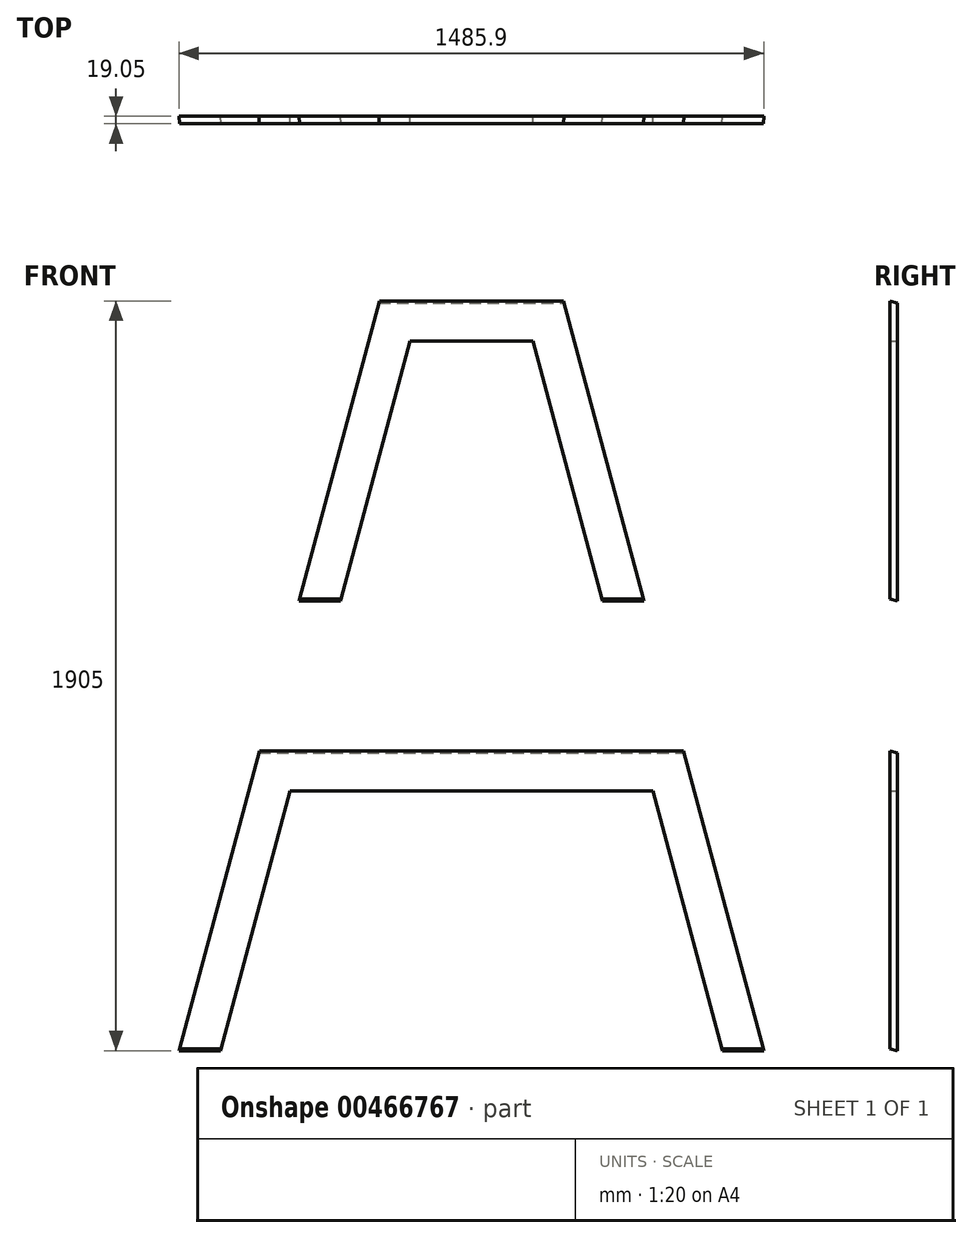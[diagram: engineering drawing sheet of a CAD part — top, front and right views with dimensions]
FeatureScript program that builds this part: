
annotation { "Feature Type Name" : "Feature", "Feature Type Description" : "" }
export const myFeature = defineFeature(function(context is Context, id is Id, definition is map)
    precondition{}
    {
        {
            var Q0;
            Q0=qCreatedBy(makeId("Front.planeOp"),FACE);
            var sketch = newSketch(context, id + "F0", { "sketchPlane" : qUnion([Q0])});
            skLineSegment(sketch, "E0", {"start": v(-742.95, -762) * mm, "end": v(-538.77, 0) * mm});
            skLineSegment(sketch, "E1", {"start": v(-538.77, 0) * mm, "end": v(0, 0) * mm});
            skLineSegment(sketch, "E2", {"start": v(-742.95, -762) * mm, "end": v(-637.77, -762) * mm});
            skLineSegment(sketch, "E3", {"start": v(-637.77, -762) * mm, "end": v(-460.81, -101.6) * mm});
            skLineSegment(sketch, "E4", {"start": v(-460.81, -101.6) * mm, "end": v(0, -101.6) * mm});
            skLineSegment(sketch, "E5", {"start": v(0, -101.6) * mm, "end": v(0, -310.28) * mm, "construction": true});
            skLineSegment(sketch, "E6.MirrorCS", {"start": v(460.81, -101.6) * mm, "end": v(0, -101.6) * mm});
            skLineSegment(sketch, "E7.MirrorCS", {"start": v(538.77, 0) * mm, "end": v(0, 0) * mm});
            skLineSegment(sketch, "E8.MirrorCS", {"start": v(742.95, -762) * mm, "end": v(538.77, 0) * mm});
            skLineSegment(sketch, "E9.MirrorCS", {"start": v(742.95, -762) * mm, "end": v(637.77, -762) * mm});
            skLineSegment(sketch, "E10.MirrorCS", {"start": v(637.77, -762) * mm, "end": v(460.81, -101.6) * mm});
            skLineSegment(sketch, "E11", {"start": v(-742.95, -762) * mm, "end": v(-742.95, -436.33) * mm, "construction": true});
            skSolve(sketch);
        }
        {
            var Q0;
            Q0 = qSketchRegion(id + "F0", true);
            extrude(context, id + "F1", {"entities" : qUnion([Q0]), "depth" : 19.05 * mm, "offsetDistance" : 25.4 * mm});
        }
        {
            var Q0;
            Q0=qCreatedBy(makeId("Front.planeOp"),FACE);
            var sketch = newSketch(context, id + "F2", { "sketchPlane" : qUnion([Q0])});
            skLineSegment(sketch, "E12", {"start": v(0, 1041.4) * mm, "end": v(-156.01, 1041.4) * mm});
            skLineSegment(sketch, "E13", {"start": v(-156.01, 1041.4) * mm, "end": v(-332.97, 381) * mm});
            skLineSegment(sketch, "E14", {"start": v(-332.97, 381) * mm, "end": v(-438.15, 381) * mm});
            skLineSegment(sketch, "E15", {"start": v(-233.97, 1143) * mm, "end": v(0, 1143) * mm});
            skLineSegment(sketch, "E16", {"start": v(-233.97, 1143) * mm, "end": v(-438.15, 381) * mm});
            skLineSegment(sketch, "E17", {"start": v(0, 1041.4) * mm, "end": v(0, 675.06) * mm, "construction": true});
            skLineSegment(sketch, "E18.MirrorCS", {"start": v(0, 1041.4) * mm, "end": v(156.01, 1041.4) * mm});
            skLineSegment(sketch, "E19.MirrorCS", {"start": v(156.01, 1041.4) * mm, "end": v(332.97, 381) * mm});
            skLineSegment(sketch, "E20.MirrorCS", {"start": v(332.97, 381) * mm, "end": v(438.15, 381) * mm});
            skLineSegment(sketch, "E21.MirrorCS", {"start": v(233.97, 1143) * mm, "end": v(438.15, 381) * mm});
            skLineSegment(sketch, "E22.MirrorCS", {"start": v(233.97, 1143) * mm, "end": v(0, 1143) * mm});
            skLineSegment(sketch, "E23", {"start": v(-438.15, 381) * mm, "end": v(-438.15, 831.6) * mm, "construction": true});
            skSolve(sketch);
        }
        {
            var Q0;
            Q0 = qSketchRegion(id + "F2", true);
            extrude(context, id + "F3", {"entities" : qUnion([Q0]), "depth" : 19.05 * mm, "offsetDistance" : 25.4 * mm});
        }
        {
            var Q0;
            Q0=qCreatedBy(makeId("Right.planeOp"),FACE);
            var sketch = newSketch(context, id + "F4", { "sketchPlane" : qUnion([Q0])});
            skLineSegment(sketch, "E24", {"start": v(-19.05, -762) * mm, "end": v(0, -762) * mm});
            skLineSegment(sketch, "E25", {"start": v(0, -762) * mm, "end": v(-19.05, -756.9) * mm});
            skLineSegment(sketch, "E26", {"start": v(-19.05, -756.9) * mm, "end": v(-19.05, -762) * mm});
            skPoint(sketch, "E27.orphan", {"position": v(-19.05, -807.55) * mm});
            skLineSegment(sketch, "E28", {"start": v(0, 0) * mm, "end": v(-19.05, 0) * mm});
            skLineSegment(sketch, "E29", {"start": v(-19.05, 0) * mm, "end": v(0, -5.1) * mm});
            skLineSegment(sketch, "E30", {"start": v(0, -5.1) * mm, "end": v(0, 0) * mm});
            skLineSegment(sketch, "E31", {"start": v(0, 381) * mm, "end": v(-19.05, 381) * mm});
            skLineSegment(sketch, "E32", {"start": v(-19.05, 381) * mm, "end": v(-19.05, 386.1) * mm});
            skLineSegment(sketch, "E33", {"start": v(-19.05, 386.1) * mm, "end": v(0, 381) * mm});
            skLineSegment(sketch, "E34", {"start": v(-19.05, 1143) * mm, "end": v(0, 1143) * mm});
            skLineSegment(sketch, "E35", {"start": v(0, 1143) * mm, "end": v(0, 1137.9) * mm});
            skLineSegment(sketch, "E36", {"start": v(0, 1137.9) * mm, "end": v(-19.05, 1143) * mm});
            skSolve(sketch);
        }
        {
            var Q0;
            Q0 = qSketchRegion(id + "F4", true);
            extrude(context, id + "F5", {"entities" : qUnion([Q0]), "operationType" : NewBodyOperationType.REMOVE, "endBound" : BoundingType.SYMMETRIC, "oppositeDirection" : true, "depth" : 1524 * mm, "offsetDistance" : 25.4 * mm});
        }
    });
